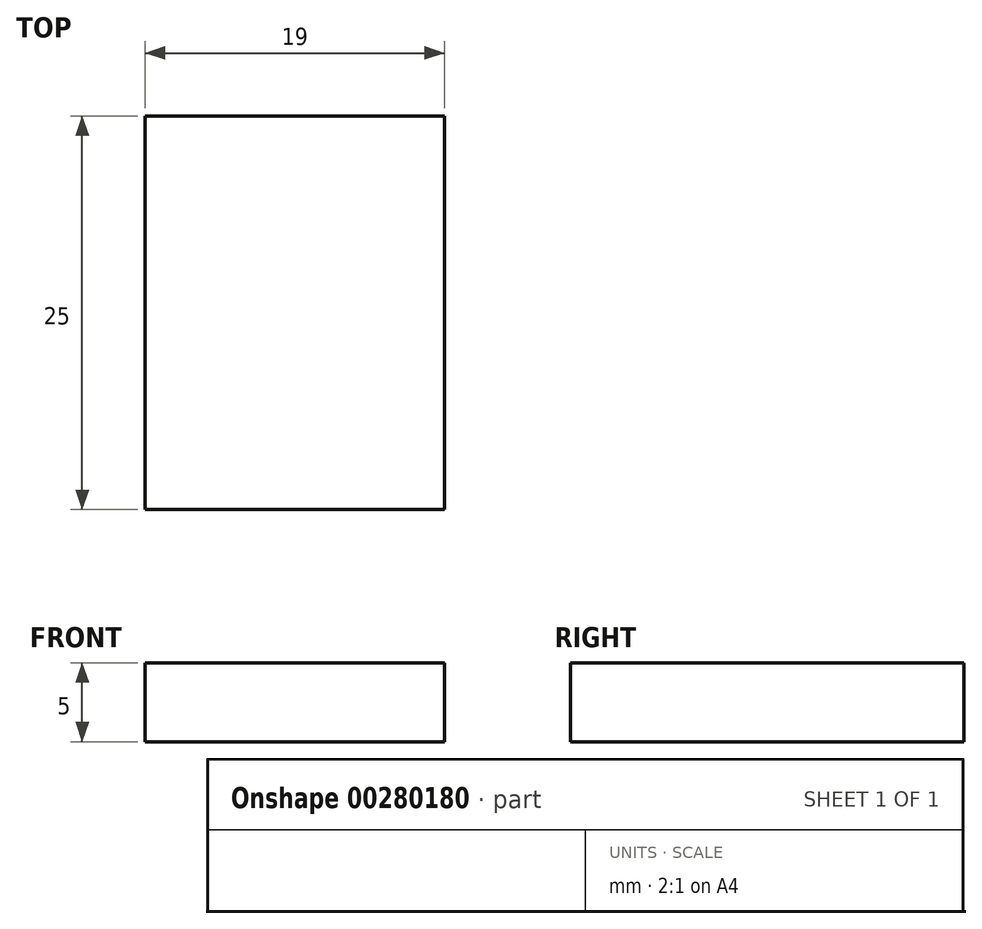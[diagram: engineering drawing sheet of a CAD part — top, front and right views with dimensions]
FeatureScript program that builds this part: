
annotation { "Feature Type Name" : "Feature", "Feature Type Description" : "" }
export const myFeature = defineFeature(function(context is Context, id is Id, definition is map)
    precondition{}
    {
        {
            var Q0;
            Q0=qCreatedBy(makeId("Front.planeOp"),FACE);
            var sketch = newSketch(context, id + "F0", { "sketchPlane" : qUnion([Q0])});
            skLineSegment(sketch, "E0.bottom", {"start": v(9.5, -2.5) * mm, "end": v(-9.5, -2.5) * mm});
            skLineSegment(sketch, "E0.top", {"start": v(9.5, 2.5) * mm, "end": v(-9.5, 2.5) * mm});
            skLineSegment(sketch, "E0.left", {"start": v(9.5, -2.5) * mm, "end": v(9.5, 2.5) * mm});
            skLineSegment(sketch, "E0.right", {"start": v(-9.5, -2.5) * mm, "end": v(-9.5, 2.5) * mm});
            skPoint(sketch, "E0.middle", {"position": v(0, 0) * mm});
            skSolve(sketch);
        }
        {
            var Q0;
            Q0 = qSketchRegion(id + "F0", true);
            extrude(context, id + "F1", {"entities" : qUnion([Q0]), "depth" : 25 * mm, "symmetric" : true});
        }
    });
